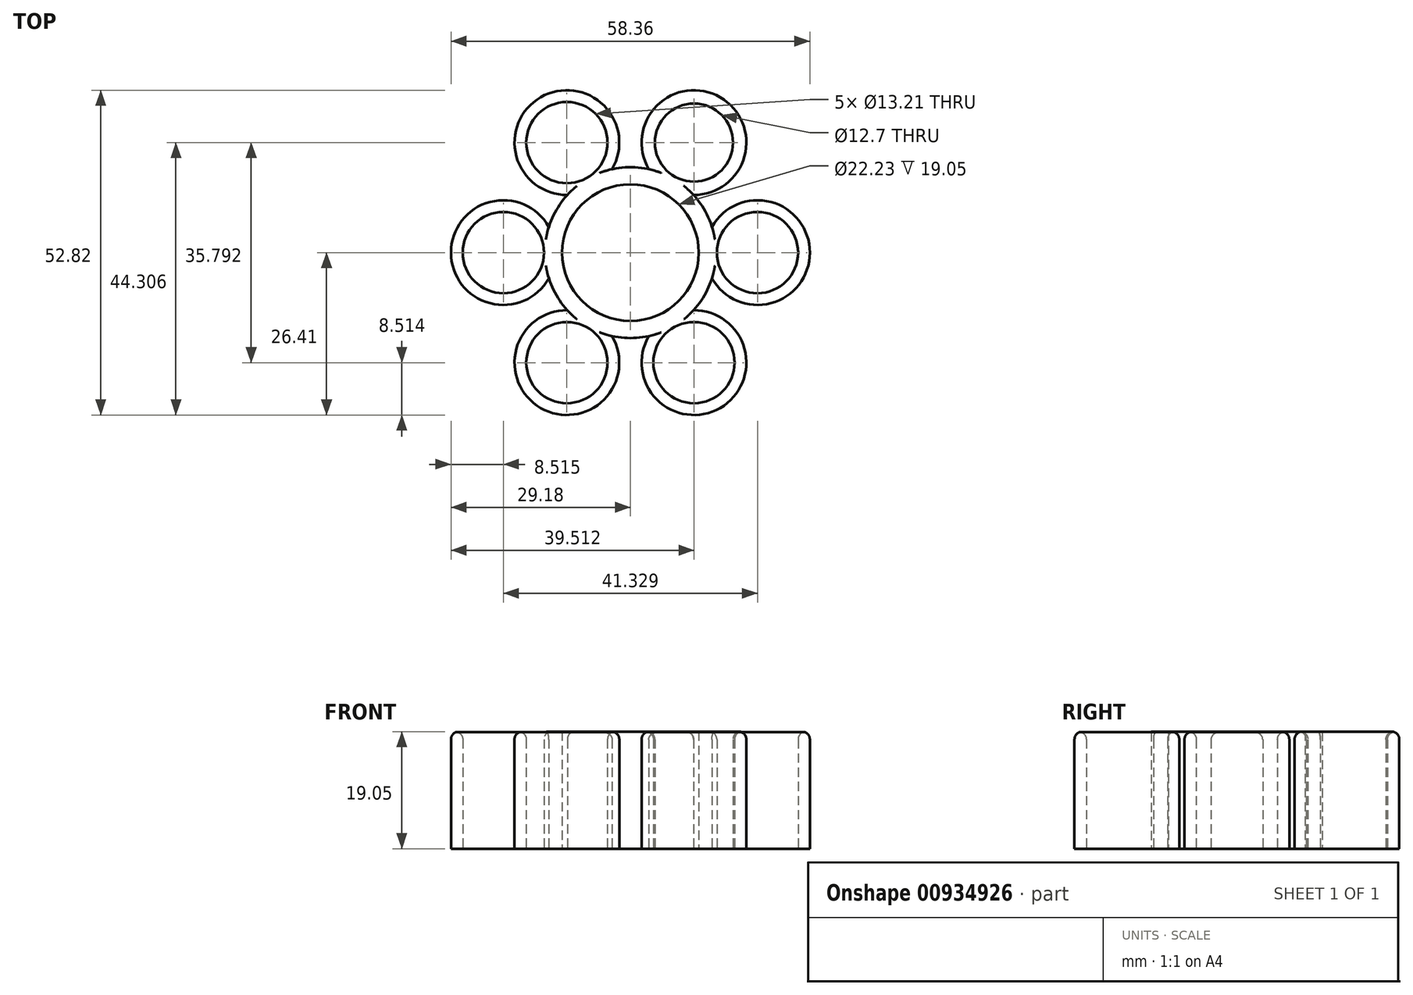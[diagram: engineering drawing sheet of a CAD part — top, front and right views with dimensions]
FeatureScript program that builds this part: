
annotation { "Feature Type Name" : "Feature", "Feature Type Description" : "" }
export const myFeature = defineFeature(function(context is Context, id is Id, definition is map)
    precondition{}
    {
        {
            var Q0;
            Q0=qCreatedBy(makeId("Top.planeOp"),FACE);
            var sketch = newSketch(context, id + "F0", { "sketchPlane" : qUnion([Q0])});
            skCircle(sketch, "E0", {"center": v(0, 0) * mm, "radius": 11.11 * mm});
            skCircle(sketch, "E1.cCircle", {"center": v(0, 0) * mm, "radius": 10.32 * mm, "construction": true});
            skCircle(sketch, "E2.cCircle", {"center": v(0, 0) * mm, "radius": 20.66 * mm, "construction": true});
            skCircle(sketch, "E3", {"center": v(-10.33, 17.9) * mm, "radius": 6.6 * mm});
            skCircle(sketch, "E4", {"center": v(10.33, 17.9) * mm, "radius": 6.35 * mm});
            skCircle(sketch, "E5", {"center": v(20.66, 0) * mm, "radius": 6.6 * mm});
            skCircle(sketch, "E6", {"center": v(10.33, -17.9) * mm, "radius": 6.6 * mm});
            skCircle(sketch, "E7", {"center": v(-10.33, -17.9) * mm, "radius": 6.6 * mm});
            skCircle(sketch, "E8", {"center": v(-20.66, 0) * mm, "radius": 6.6 * mm});
            skCircle(sketch, "E9", {"center": v(-10.33, 17.9) * mm, "radius": 8.52 * mm});
            skCircle(sketch, "E10", {"center": v(10.33, 17.9) * mm, "radius": 8.52 * mm});
            skCircle(sketch, "E11", {"center": v(20.66, 0) * mm, "radius": 8.52 * mm});
            skCircle(sketch, "E12", {"center": v(10.33, -17.9) * mm, "radius": 8.52 * mm});
            skCircle(sketch, "E13", {"center": v(-10.33, -17.9) * mm, "radius": 8.52 * mm});
            skCircle(sketch, "E14", {"center": v(-20.66, 0) * mm, "radius": 8.52 * mm});
            skCircle(sketch, "E15", {"center": v(0, 0) * mm, "radius": 13.9 * mm});
            skSolve(sketch);
        }
        {
            var Q0;
            Q0=makeQuery(id+"F0.imprint","IMPRINT",FACE,{"disambiguationData":[TD([[makeQuery(id+"F0.imprint","IMPRINT",EDGE,{"derivedFrom":sQuery(id+"F0.wireOp",EDGE,"E3")}),-1.0]])]});
            var Q1;
            {var subQ0=sQuery(id+"F0.wireOp",EDGE,"E15");var subQ1=sQuery(id+"F0.wireOp",EDGE,"E9");var subQ2=makeQuery(id+"F0.imprint","INTERSECT",VERTEX,{"disambiguationData":[OD(0.0)],"derivedFrom":[subQ1,subQ0]});Q1=makeQuery(id+"F0.imprint","IMPRINT",FACE,{"disambiguationData":[TD([[makeQuery(id+"F0.imprint","IMPRINT",EDGE,{"disambiguationData":[TD([[subQ2,1.0]])],"derivedFrom":subQ1}),1.0]])]});}
            var Q2;
            Q2=makeQuery(id+"F0.imprint","IMPRINT",FACE,{"disambiguationData":[TD([[makeQuery(id+"F0.imprint","IMPRINT",EDGE,{"derivedFrom":sQuery(id+"F0.wireOp",EDGE,"E0")}),-1.0]])]});
            var Q3;
            {var subQ0=sQuery(id+"F0.wireOp",EDGE,"E15");var subQ1=sQuery(id+"F0.wireOp",EDGE,"E10");var subQ2=makeQuery(id+"F0.imprint","INTERSECT",VERTEX,{"disambiguationData":[OD(0.0)],"derivedFrom":[subQ1,subQ0]});Q3=makeQuery(id+"F0.imprint","IMPRINT",FACE,{"disambiguationData":[TD([[makeQuery(id+"F0.imprint","IMPRINT",EDGE,{"disambiguationData":[TD([[subQ2,1.0]])],"derivedFrom":subQ1}),1.0]])]});}
            var Q4;
            {var subQ0=sQuery(id+"F0.wireOp",EDGE,"E15");var subQ1=sQuery(id+"F0.wireOp",EDGE,"E11");var subQ2=makeQuery(id+"F0.imprint","INTERSECT",VERTEX,{"disambiguationData":[OD(0.0)],"derivedFrom":[subQ1,subQ0]});Q4=makeQuery(id+"F0.imprint","IMPRINT",FACE,{"disambiguationData":[TD([[makeQuery(id+"F0.imprint","IMPRINT",EDGE,{"disambiguationData":[TD([[subQ2,-1.0]])],"derivedFrom":subQ1}),1.0]])]});}
            var Q5;
            {var subQ0=sQuery(id+"F0.wireOp",EDGE,"E15");var subQ1=sQuery(id+"F0.wireOp",EDGE,"E12");var subQ2=makeQuery(id+"F0.imprint","INTERSECT",VERTEX,{"disambiguationData":[OD(0.0)],"derivedFrom":[subQ1,subQ0]});Q5=makeQuery(id+"F0.imprint","IMPRINT",FACE,{"disambiguationData":[TD([[makeQuery(id+"F0.imprint","IMPRINT",EDGE,{"disambiguationData":[TD([[subQ2,1.0]])],"derivedFrom":subQ1}),1.0]])]});}
            var Q6;
            {var subQ0=sQuery(id+"F0.wireOp",EDGE,"E15");var subQ1=sQuery(id+"F0.wireOp",EDGE,"E13");var subQ2=makeQuery(id+"F0.imprint","INTERSECT",VERTEX,{"disambiguationData":[OD(0.0)],"derivedFrom":[subQ1,subQ0]});Q6=makeQuery(id+"F0.imprint","IMPRINT",FACE,{"disambiguationData":[TD([[makeQuery(id+"F0.imprint","IMPRINT",EDGE,{"disambiguationData":[TD([[subQ2,1.0]])],"derivedFrom":subQ1}),1.0]])]});}
            var Q7;
            {var subQ0=sQuery(id+"F0.wireOp",EDGE,"E15");var subQ1=sQuery(id+"F0.wireOp",EDGE,"E14");var subQ2=makeQuery(id+"F0.imprint","INTERSECT",VERTEX,{"disambiguationData":[OD(0.0)],"derivedFrom":[subQ1,subQ0]});Q7=makeQuery(id+"F0.imprint","IMPRINT",FACE,{"disambiguationData":[TD([[makeQuery(id+"F0.imprint","IMPRINT",EDGE,{"disambiguationData":[TD([[subQ2,1.0]])],"derivedFrom":subQ1}),1.0]])]});}
            var Q8;
            Q8=makeQuery(id+"F0.imprint","IMPRINT",FACE,{"disambiguationData":[TD([[makeQuery(id+"F0.imprint","IMPRINT",EDGE,{"derivedFrom":sQuery(id+"F0.wireOp",EDGE,"E8")}),-1.0]])]});
            var Q9;
            Q9=makeQuery(id+"F0.imprint","IMPRINT",FACE,{"disambiguationData":[TD([[makeQuery(id+"F0.imprint","IMPRINT",EDGE,{"derivedFrom":sQuery(id+"F0.wireOp",EDGE,"E4")}),-1.0]])]});
            var Q10;
            Q10=makeQuery(id+"F0.imprint","IMPRINT",FACE,{"disambiguationData":[TD([[makeQuery(id+"F0.imprint","IMPRINT",EDGE,{"derivedFrom":sQuery(id+"F0.wireOp",EDGE,"E5")}),-1.0]])]});
            var Q11;
            Q11=makeQuery(id+"F0.imprint","IMPRINT",FACE,{"disambiguationData":[TD([[makeQuery(id+"F0.imprint","IMPRINT",EDGE,{"derivedFrom":sQuery(id+"F0.wireOp",EDGE,"E6")}),-1.0]])]});
            var Q12;
            Q12=makeQuery(id+"F0.imprint","IMPRINT",FACE,{"disambiguationData":[TD([[makeQuery(id+"F0.imprint","IMPRINT",EDGE,{"derivedFrom":sQuery(id+"F0.wireOp",EDGE,"E7")}),-1.0]])]});
            extrude(context, id + "F1", {"entities" : qUnion([Q0, Q1, Q2, Q3, Q4, Q5, Q6, Q7, Q8, Q9, Q10, Q11, Q12]), "depth" : 19.05 * mm, "offsetDistance" : 25.4 * mm});
        }
        {
            var Q0;
            Q0=makeQuery(id+"F1.opExtrude","CAP_EDGE",EDGE,{"disambiguationData":[OSD([sQuery(id+"F0.wireOp",EDGE,"E14")])],"isStart":false});
            var Q1;
            Q1=makeQuery(id+"F1.opExtrude","CAP_EDGE",EDGE,{"disambiguationData":[OSD([sQuery(id+"F0.wireOp",EDGE,"E9")])],"isStart":false});
            var Q2;
            Q2=makeQuery(id+"F1.opExtrude","CAP_EDGE",EDGE,{"disambiguationData":[OSD([sQuery(id+"F0.wireOp",EDGE,"E10")])],"isStart":false});
            var Q3;
            Q3=makeQuery(id+"F1.opExtrude","CAP_EDGE",EDGE,{"disambiguationData":[OSD([sQuery(id+"F0.wireOp",EDGE,"E13")])],"isStart":false});
            var Q4;
            Q4=makeQuery(id+"F1.opExtrude","CAP_EDGE",EDGE,{"disambiguationData":[OSD([sQuery(id+"F0.wireOp",EDGE,"E12")])],"isStart":false});
            var Q5;
            Q5=makeQuery(id+"F1.opExtrude","CAP_EDGE",EDGE,{"disambiguationData":[OSD([sQuery(id+"F0.wireOp",EDGE,"E11")])],"isStart":false});
            fillet(context, id + "F2", {"entities" : qUnion([Q0, Q1, Q2, Q3, Q4, Q5]), "radius" : 1.27 * mm, "tangentPropagation" : true, "allowEdgeOverflow" : false});
        }
        {
            var Q0;
            Q0=makeQuery(id+"F1.opExtrude","CAP_EDGE",EDGE,{"disambiguationData":[OSD([sQuery(id+"F0.wireOp",EDGE,"E8")])],"isStart":false});
            var Q1;
            Q1=makeQuery(id+"F1.opExtrude","CAP_EDGE",EDGE,{"disambiguationData":[OSD([sQuery(id+"F0.wireOp",EDGE,"E3")])],"isStart":false});
            var Q2;
            Q2=makeQuery(id+"F1.opExtrude","CAP_EDGE",EDGE,{"disambiguationData":[OSD([sQuery(id+"F0.wireOp",EDGE,"E4")])],"isStart":false});
            var Q3;
            Q3=makeQuery(id+"F1.opExtrude","CAP_EDGE",EDGE,{"disambiguationData":[OSD([sQuery(id+"F0.wireOp",EDGE,"E5")])],"isStart":false});
            var Q4;
            Q4=makeQuery(id+"F1.opExtrude","CAP_EDGE",EDGE,{"disambiguationData":[OSD([sQuery(id+"F0.wireOp",EDGE,"E6")])],"isStart":false});
            var Q5;
            Q5=makeQuery(id+"F1.opExtrude","CAP_EDGE",EDGE,{"disambiguationData":[OSD([sQuery(id+"F0.wireOp",EDGE,"E7")])],"isStart":false});
            fillet(context, id + "F3", {"entities" : qUnion([Q0, Q1, Q2, Q3, Q4, Q5]), "radius" : 1.27 * mm, "tangentPropagation" : true, "allowEdgeOverflow" : false});
        }
        {
            var Q0;
            Q0=makeQuery(id+"F3.opFillet","BLEND_EDGE",EDGE,{"blendedFrom":[makeQuery(id+"F1.opExtrude","CAP_EDGE",EDGE,{"disambiguationData":[OSD([sQuery(id+"F0.wireOp",EDGE,"E7")])],"isStart":false}),makeQuery(id+"F2.opFillet","BLEND_FACE",FACE,{"disambiguationData":[OSD([sQuery(id+"F0.wireOp",EDGE,"E13")])]})],"blendedInto":[makeQuery(id+"F2.opFillet","BLEND_FACE",FACE,{"disambiguationData":[OSD([sQuery(id+"F0.wireOp",EDGE,"E13")])]})]});
            var Q1;
            Q1=makeQuery(id+"F3.opFillet","BLEND_EDGE",EDGE,{"blendedFrom":[makeQuery(id+"F1.opExtrude","CAP_EDGE",EDGE,{"disambiguationData":[OSD([sQuery(id+"F0.wireOp",EDGE,"E8")])],"isStart":false}),makeQuery(id+"F2.opFillet","BLEND_FACE",FACE,{"disambiguationData":[OSD([sQuery(id+"F0.wireOp",EDGE,"E14")])]})],"blendedInto":[makeQuery(id+"F2.opFillet","BLEND_FACE",FACE,{"disambiguationData":[OSD([sQuery(id+"F0.wireOp",EDGE,"E14")])]})]});
            var Q2;
            Q2=makeQuery(id+"F3.opFillet","BLEND_EDGE",EDGE,{"blendedFrom":[makeQuery(id+"F1.opExtrude","CAP_EDGE",EDGE,{"disambiguationData":[OSD([sQuery(id+"F0.wireOp",EDGE,"E3")])],"isStart":false}),makeQuery(id+"F2.opFillet","BLEND_FACE",FACE,{"disambiguationData":[OSD([sQuery(id+"F0.wireOp",EDGE,"E9")])]})],"blendedInto":[makeQuery(id+"F2.opFillet","BLEND_FACE",FACE,{"disambiguationData":[OSD([sQuery(id+"F0.wireOp",EDGE,"E9")])]})]});
            var Q3;
            Q3=makeQuery(id+"F3.opFillet","BLEND_EDGE",EDGE,{"blendedFrom":[makeQuery(id+"F1.opExtrude","CAP_EDGE",EDGE,{"disambiguationData":[OSD([sQuery(id+"F0.wireOp",EDGE,"E4")])],"isStart":false}),makeQuery(id+"F2.opFillet","BLEND_FACE",FACE,{"disambiguationData":[OSD([sQuery(id+"F0.wireOp",EDGE,"E10")])]})],"blendedInto":[makeQuery(id+"F2.opFillet","BLEND_FACE",FACE,{"disambiguationData":[OSD([sQuery(id+"F0.wireOp",EDGE,"E10")])]})]});
            var Q4;
            Q4=makeQuery(id+"F3.opFillet","BLEND_EDGE",EDGE,{"blendedFrom":[makeQuery(id+"F1.opExtrude","CAP_EDGE",EDGE,{"disambiguationData":[OSD([sQuery(id+"F0.wireOp",EDGE,"E5")])],"isStart":false}),makeQuery(id+"F2.opFillet","BLEND_FACE",FACE,{"disambiguationData":[OSD([sQuery(id+"F0.wireOp",EDGE,"E11")])]})],"blendedInto":[makeQuery(id+"F2.opFillet","BLEND_FACE",FACE,{"disambiguationData":[OSD([sQuery(id+"F0.wireOp",EDGE,"E11")])]})]});
            var Q5;
            Q5=makeQuery(id+"F3.opFillet","BLEND_EDGE",EDGE,{"blendedFrom":[makeQuery(id+"F1.opExtrude","CAP_EDGE",EDGE,{"disambiguationData":[OSD([sQuery(id+"F0.wireOp",EDGE,"E6")])],"isStart":false}),makeQuery(id+"F2.opFillet","BLEND_FACE",FACE,{"disambiguationData":[OSD([sQuery(id+"F0.wireOp",EDGE,"E12")])]})],"blendedInto":[makeQuery(id+"F2.opFillet","BLEND_FACE",FACE,{"disambiguationData":[OSD([sQuery(id+"F0.wireOp",EDGE,"E12")])]})]});
            fillet(context, id + "F4", {"entities" : qUnion([Q0, Q1, Q2, Q3, Q4, Q5]), "radius" : 0.64 * mm, "tangentPropagation" : true, "allowEdgeOverflow" : false});
        }
    });
